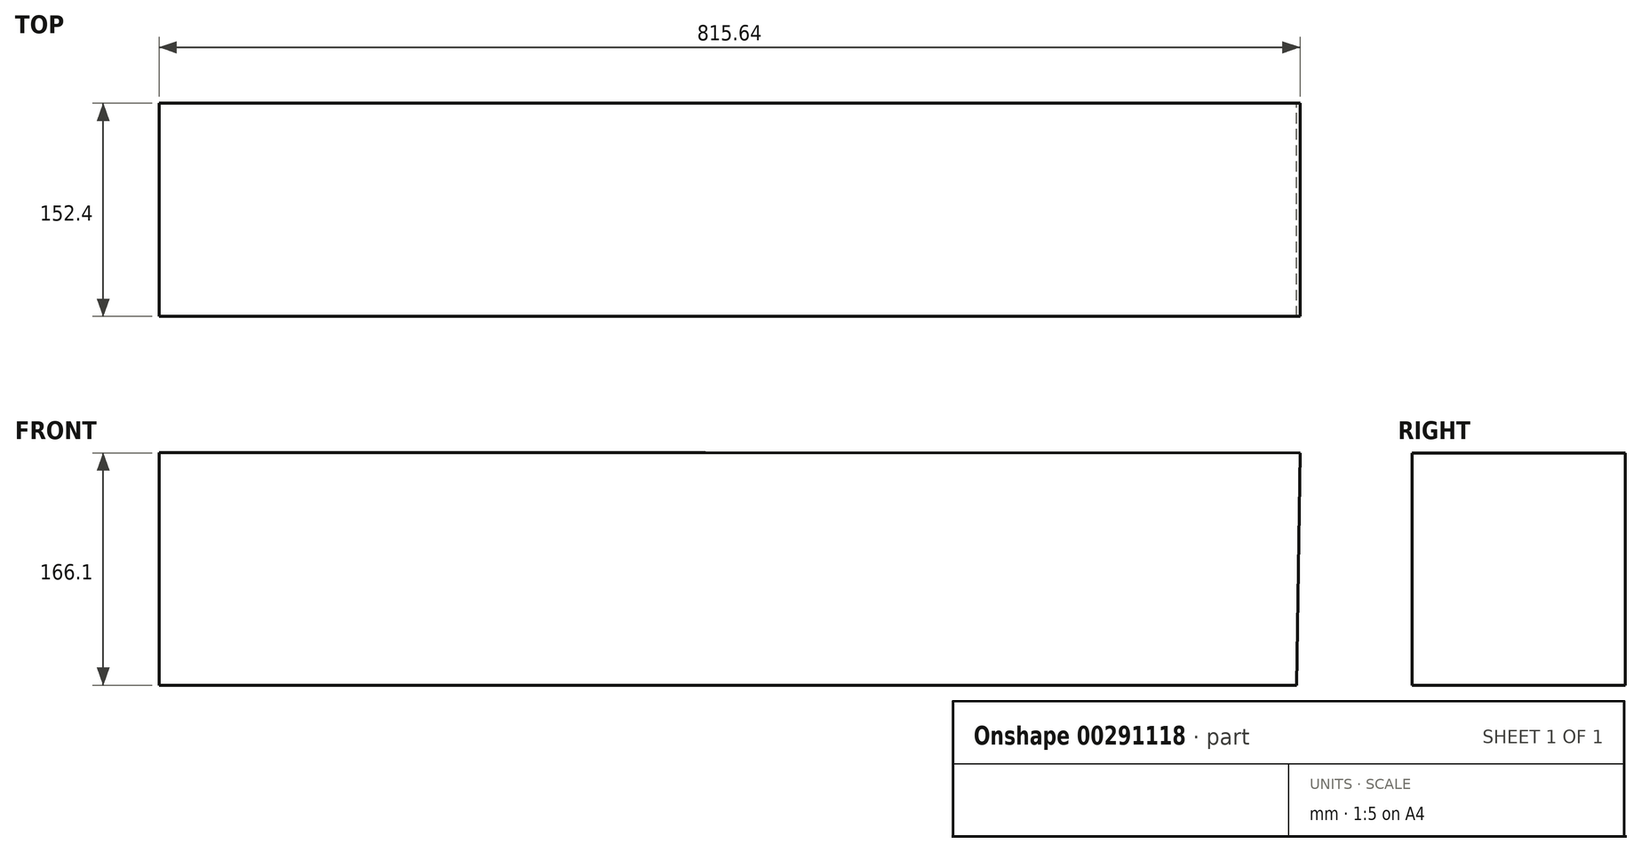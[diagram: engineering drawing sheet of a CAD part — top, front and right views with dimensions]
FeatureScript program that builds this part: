
annotation { "Feature Type Name" : "Feature", "Feature Type Description" : "" }
export const myFeature = defineFeature(function(context is Context, id is Id, definition is map)
    precondition{}
    {
        {
            var Q0;
            Q0=qCreatedBy(makeId("Front.planeOp"),FACE);
            var sketch = newSketch(context, id + "F0", { "sketchPlane" : qUnion([Q0])});
            skLineSegment(sketch, "E0", {"start": v(0, 0) * mm, "end": v(-390.5, 0) * mm});
            skLineSegment(sketch, "E1", {"start": v(-11.16, 0) * mm, "end": v(422.87, 0) * mm});
            skLineSegment(sketch, "E2", {"start": v(-390.5, 0) * mm, "end": v(-390.5, 166.1) * mm});
            skLineSegment(sketch, "E3", {"start": v(-390.5, 166.1) * mm, "end": v(0, 166.1) * mm});
            skLineSegment(sketch, "E4", {"start": v(0, 166.1) * mm, "end": v(425.15, 166.09) * mm});
            skLineSegment(sketch, "E5", {"start": v(422.87, 0) * mm, "end": v(425.15, 166.09) * mm});
            skSolve(sketch);
        }
        {
            var Q0;
            {var subQ1=sQuery(id+"F0.wireOp",EDGE,"E0");Q0=makeQuery(id+"F0.imprint","IMPRINT",FACE,{"disambiguationData":[TD([[makeQuery(id+"F0.imprint","IMPRINT",EDGE,{"derivedFrom":subQ1}),-1.0]])]});}
            extrude(context, id + "F1", {"entities" : qUnion([Q0]), "depth" : 152.4 * mm});
        }
    });
